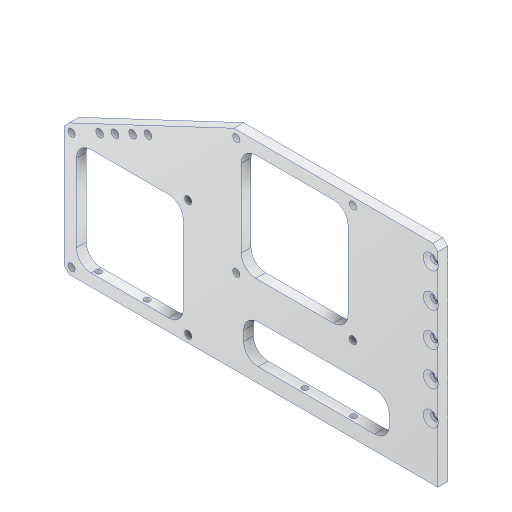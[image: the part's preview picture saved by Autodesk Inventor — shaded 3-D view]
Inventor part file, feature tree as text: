
AUTODESK INVENTOR PART (.ipt)
format: ipt  version: 2023.2 (Build 272271000, 271)  size: 440,320 bytes
history: native  units: mm
features: extrude x9, sketch x9, projected_geometry x6, chamfer x3, fillet x2, other x1
ambient origin geometry x8: Origin, YZ Plane, XZ Plane, XY Plane, X Axis, Y Axis, Z Axis, Center Point
bodies: Body1 (feature_tree)
feature tree (30):
  other  "솔리드1"
  extrude  "돌출1"  Depth=4.0mm TaperAngle=0.0deg
  extrude  "돌출4"  Depth=75.0mm
  extrude  "돌출5"  Depth=32.0mm
  extrude  "돌출6"  Depth=4.0mm TaperAngle=0.0deg
  extrude  "돌출7"  Depth=4.0mm TaperAngle=0.0deg
  fillet  "모깎기1"  Radius=32.0mm
  extrude  "돌출8"  Depth=4.0mm TaperAngle=0.0deg
  extrude  "돌출9"  Depth=5.5mm
  fillet  "모깎기2"  Radius=6.0mm
  extrude  "돌출10"  TaperAngle=90.0deg  [1 undecoded]
  chamfer  "모따기1"  Distance=36.0mm
  chamfer  "모따기2"  Distance=3.2mm
  chamfer  "모따기3"  Distance=3.2mm
  extrude  "돌출11"  Depth=3.2mm
  sketch  "스케치1"
  sketch  "스케치3"
  projected_geometry  "투영된 루프1"
  sketch  "스케치6"
  projected_geometry  "투영된 루프3"
  sketch  "스케치9"
  projected_geometry  "투영된 루프4"
  sketch  "스케치10"
  sketch  "스케치11"
  projected_geometry  "투영된 루프5"
  sketch  "스케치12"
  projected_geometry  "투영된 루프6"
  sketch  "스케치13"
  sketch  "스케치14"
  projected_geometry  "투영된 루프7"
note: 1 required parameter value undecoded (feature->parameter linkage not recoverable at this tier; creation-order binding heuristic only, values carry confidence <= 0.55)
